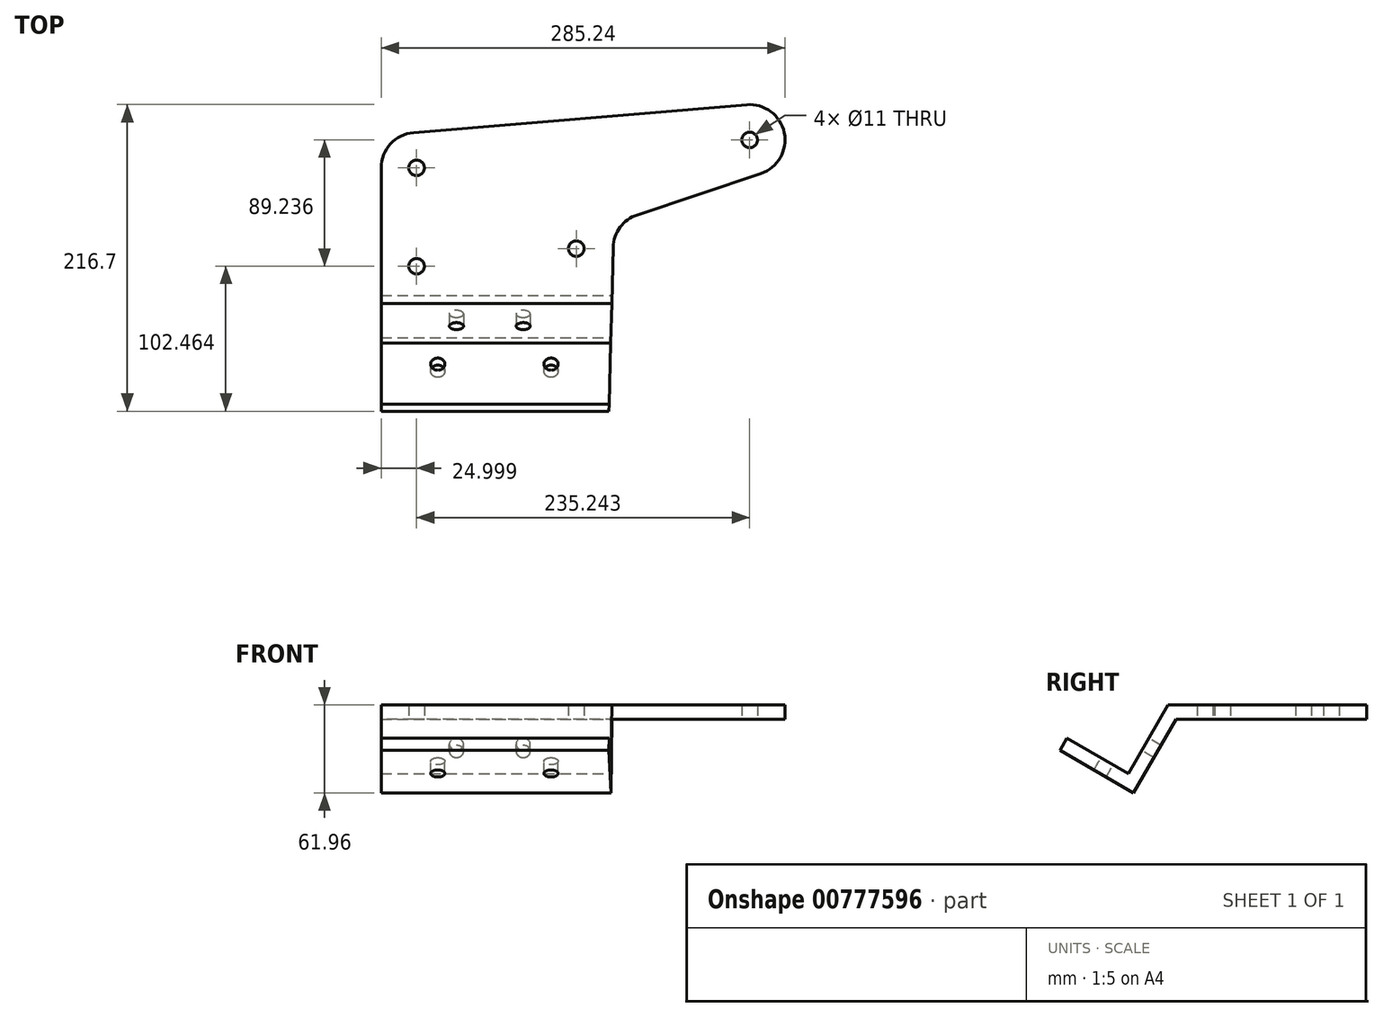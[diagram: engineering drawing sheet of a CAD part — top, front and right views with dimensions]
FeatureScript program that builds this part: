
annotation { "Feature Type Name" : "Feature", "Feature Type Description" : "" }
export const myFeature = defineFeature(function(context is Context, id is Id, definition is map)
    precondition{}
    {
        {
            var Q0;
            Q0=qCreatedBy(makeId("Top.planeOp"),FACE);
            var sketch = newSketch(context, id + "F0", { "sketchPlane" : qUnion([Q0])});
            skLineSegment(sketch, "E0", {"start": v(-140.51, 0) * mm, "end": v(157, 0) * mm, "construction": true});
            skCircle(sketch, "E1", {"center": v(0, 0) * mm, "radius": 5.5 * mm});
            skCircle(sketch, "E2", {"center": v(-112.81, -12.49) * mm, "radius": 5.5 * mm});
            skCircle(sketch, "E3", {"center": v(-112.81, 57.01) * mm, "radius": 5.5 * mm});
            skCircle(sketch, "E4", {"center": v(122.43, 76.75) * mm, "radius": 5.5 * mm});
            skLineSegment(sketch, "E5", {"start": v(-137.81, 57.01) * mm, "end": v(-137.81, -32.99) * mm});
            skArc(sketch, "E6", {"start": v(-114.9, 81.93) * mm, "mid": v(-131.21, 73.94) * mm, "end": v(-137.81, 57.01) * mm});
            skArc(sketch, "E7", {"start": v(43.14, 23.89) * mm, "mid": v(30.97, 15.05) * mm, "end": v(26.07, 0.83) * mm});
            skLineSegment(sketch, "E8", {"start": v(43.14, 23.89) * mm, "end": v(130.36, 53.04) * mm});
            skLineSegment(sketch, "E9.trimOffspring", {"start": v(120.34, 101.66) * mm, "end": v(-114.9, 81.93) * mm});
            skLineSegment(sketch, "E10", {"start": v(-137.81, -32.99) * mm, "end": v(25.19, -32.99) * mm});
            skLineSegment(sketch, "E11", {"start": v(26.07, 0.83) * mm, "end": v(25.19, -32.99) * mm});
            skArc(sketch, "E12", {"start": v(130.36, 53.04) * mm, "mid": v(146.92, 81.8) * mm, "end": v(120.34, 101.66) * mm});
            skSolve(sketch);
        }
        {
            var Q0;
            Q0=makeQuery(id+"F0.imprint","IMPRINT",FACE,{"disambiguationData":[TD([[makeQuery(id+"F0.imprint","IMPRINT",EDGE,{"derivedFrom":sQuery(id+"F0.wireOp",EDGE,"E1")}),-1.0]])]});
            extrude(context, id + "F1", {"entities" : qUnion([Q0]), "depth" : 10 * mm, "offsetDistance" : 25 * mm});
        }
        {
            var Q0;
            Q0=qCreatedBy(makeId("Right.planeOp"),FACE);
            var sketch = newSketch(context, id + "F2", { "sketchPlane" : qUnion([Q0])});
            skLineSegment(sketch, "E13", {"start": v(-66.65, -38.3) * mm, "end": v(-38.76, 10) * mm});
            skLineSegment(sketch, "E14", {"start": v(-38.76, 10) * mm, "end": v(-32.99, 10) * mm});
            skLineSegment(sketch, "E15", {"start": v(-32.99, 10) * mm, "end": v(-32.99, 0) * mm});
            skLineSegment(sketch, "E16", {"start": v(-66.65, -38.3) * mm, "end": v(-109.95, -13.3) * mm});
            skLineSegment(sketch, "E17", {"start": v(-109.95, -13.3) * mm, "end": v(-114.95, -21.96) * mm});
            skLineSegment(sketch, "E18", {"start": v(-114.95, -21.96) * mm, "end": v(-62.99, -51.96) * mm});
            skLineSegment(sketch, "E19", {"start": v(-32.99, 0) * mm, "end": v(-62.99, -51.96) * mm});
            skSolve(sketch);
        }
        {
            var Q0;
            Q0 = qSketchRegion(id + "F2", true);
            var Q1;
            Q1=makeQuery(id+"F1.opExtrude","SWEPT_FACE",FACE,{"disambiguationData":[OSD([sQuery(id+"F0.wireOp",EDGE,"E5")])]});
            extrude(context, id + "F3", {"entities" : qUnion([Q0]), "operationType" : NewBodyOperationType.ADD, "endBound" : BoundingType.UP_TO_SURFACE, "oppositeDirection" : true, "depth" : 25 * mm, "endBoundEntityFace" : qUnion([Q1]), "offsetDistance" : 25 * mm});
        }
        {
            var Q0;
            Q0 = qSketchRegion(id + "F2", true);
            var Q1;
            Q1=makeQuery(id+"F1.opExtrude","SWEPT_FACE",FACE,{"disambiguationData":[OSD([sQuery(id+"F0.wireOp",EDGE,"E11")])]});
            extrude(context, id + "F4", {"entities" : qUnion([Q0]), "operationType" : NewBodyOperationType.ADD, "endBound" : BoundingType.UP_TO_SURFACE, "depth" : 25 * mm, "endBoundEntityFace" : qUnion([Q1]), "offsetDistance" : 25 * mm});
        }
        {
            var Q0;
            {var subQ0=sQuery(id+"F2.wireOp",EDGE,"E13");Q0=makeQuery(id+"F4.boolean.opBoolean","MERGE",FACE,{"derivedFrom":[makeQuery(id+"F3.opExtrude","SWEPT_FACE",FACE,{"disambiguationData":[OSD([subQ0])]}),makeQuery(id+"F4.opExtrude","SWEPT_FACE",FACE,{"disambiguationData":[OSD([subQ0])]})]});}
            var sketch = newSketch(context, id + "F5", { "sketchPlane" : qUnion([Q0])});
            skCircle(sketch, "E20", {"center": v(-84.64, -42.73) * mm, "radius": 5 * mm});
            skCircle(sketch, "E21", {"center": v(-37.48, -42.73) * mm, "radius": 5 * mm});
            skSolve(sketch);
        }
        {
            var Q0;
            Q0 = qSketchRegion(id + "F5", true);
            extrude(context, id + "F6", {"entities" : qUnion([Q0]), "operationType" : NewBodyOperationType.REMOVE, "endBound" : BoundingType.THROUGH_ALL, "oppositeDirection" : true, "depth" : 25 * mm, "offsetDistance" : 25 * mm});
        }
        {
            var Q0;
            {var subQ0=sQuery(id+"F2.wireOp",EDGE,"E16");Q0=makeQuery(id+"F4.boolean.opBoolean","MERGE",FACE,{"derivedFrom":[makeQuery(id+"F3.opExtrude","SWEPT_FACE",FACE,{"disambiguationData":[OSD([subQ0])]}),makeQuery(id+"F4.opExtrude","SWEPT_FACE",FACE,{"disambiguationData":[OSD([subQ0])]})]});}
            var sketch = newSketch(context, id + "F7", { "sketchPlane" : qUnion([Q0])});
            skCircle(sketch, "E22", {"center": v(-97.81, -55.86) * mm, "radius": 5 * mm});
            skCircle(sketch, "E23", {"center": v(-17.81, -55.86) * mm, "radius": 5 * mm});
            skLineSegment(sketch, "E24", {"start": v(-122.43, -55.86) * mm, "end": v(13.9, -55.86) * mm, "construction": true});
            skSolve(sketch);
        }
        {
            var Q0;
            Q0 = qSketchRegion(id + "F7", true);
            extrude(context, id + "F8", {"entities" : qUnion([Q0]), "operationType" : NewBodyOperationType.REMOVE, "endBound" : BoundingType.THROUGH_ALL, "oppositeDirection" : true, "depth" : 25 * mm, "offsetDistance" : 25 * mm});
        }
    });
